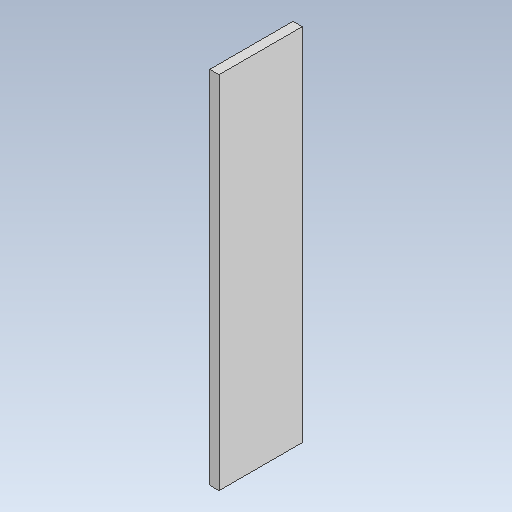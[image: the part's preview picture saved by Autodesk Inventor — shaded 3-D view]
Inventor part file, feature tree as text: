
AUTODESK INVENTOR PART (.ipt)
format: ipt  version: 2021 (Build 250183000, 183)  size: 78,336 bytes
history: native  units: mm
features: other x3, sketch x1
ambient origin geometry x8: Origin, YZ Plane, XZ Plane, XY Plane, X Axis, Y Axis, Z Axis, Center Point
bodies: Solid1 (feature_tree)
feature tree (4):
  other  "drewniany obwod.ipt"
  other  "Solid1::drewniany obwod.ipt"
  other  "TaggingFeature1"
  sketch  "Sketch1"  dims[d0=10.0mm]
